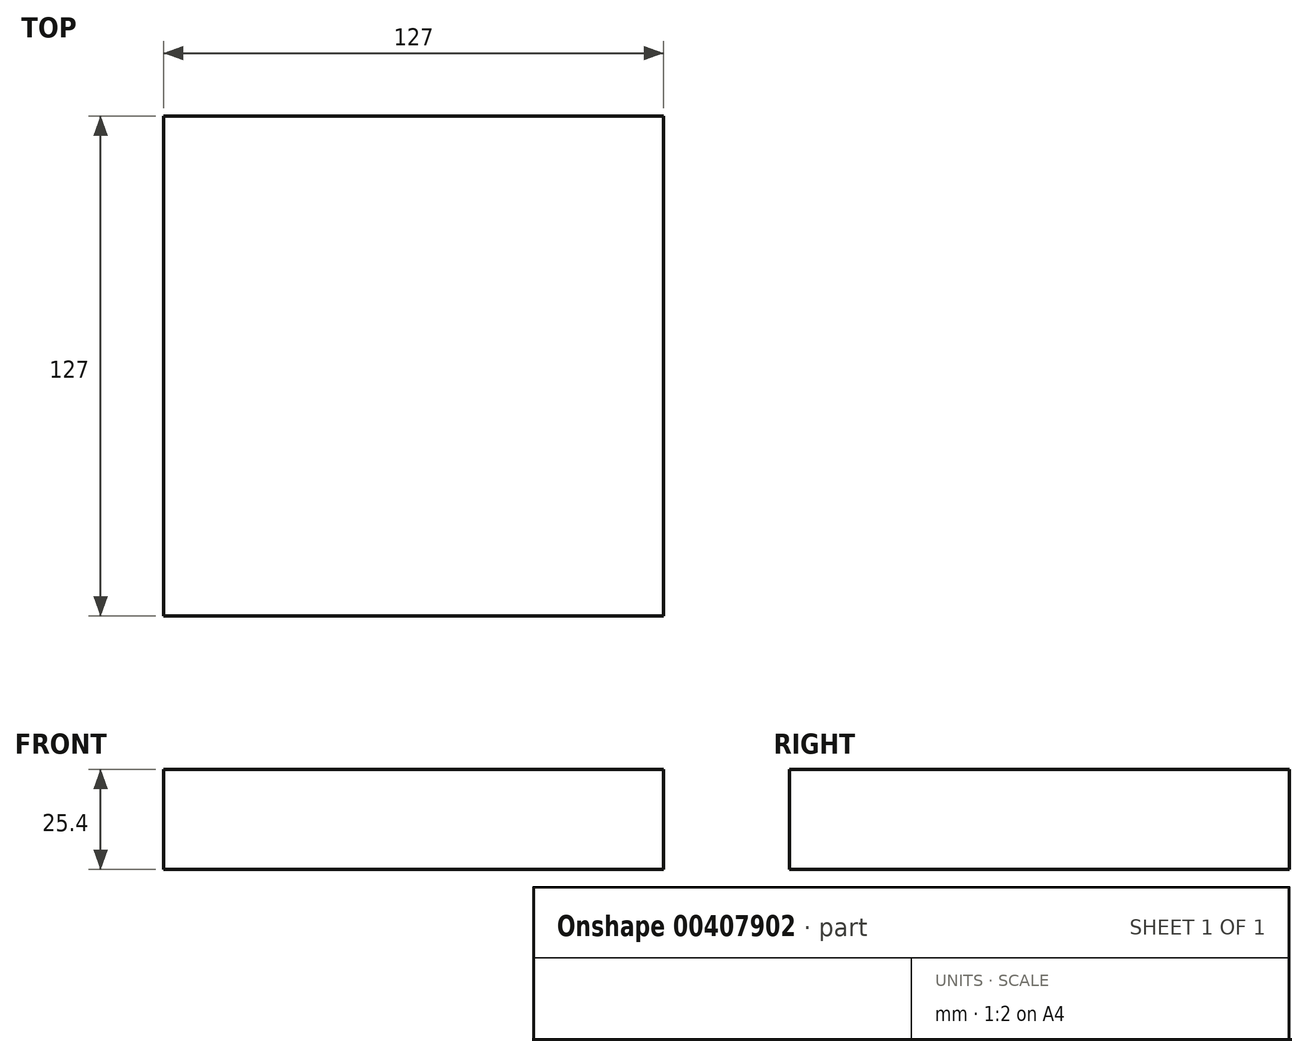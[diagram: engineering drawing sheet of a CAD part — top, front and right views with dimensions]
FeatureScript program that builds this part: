
annotation { "Feature Type Name" : "Feature", "Feature Type Description" : "" }
export const myFeature = defineFeature(function(context is Context, id is Id, definition is map)
    precondition{}
    {
        {
            var Q0;
            Q0=qCreatedBy(makeId("Top.planeOp"),FACE);
            var sketch = newSketch(context, id + "F0", { "sketchPlane" : qUnion([Q0])});
            skLineSegment(sketch, "E0", {"start": v(0, 0) * mm, "end": v(127, 0) * mm});
            skLineSegment(sketch, "E1", {"start": v(127, 0) * mm, "end": v(127, 127) * mm});
            skLineSegment(sketch, "E2", {"start": v(127, 127) * mm, "end": v(0, 127) * mm});
            skLineSegment(sketch, "E3", {"start": v(0, 127) * mm, "end": v(0, 0) * mm});
            skSolve(sketch);
        }
        {
            var Q0;
            Q0 = qSketchRegion(id + "F0", true);
            extrude(context, id + "F1", {"entities" : qUnion([Q0]), "depth" : 25.4 * mm});
        }
    });
